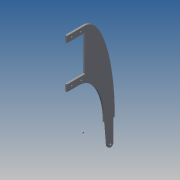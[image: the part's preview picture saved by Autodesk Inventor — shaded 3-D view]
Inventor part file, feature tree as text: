
AUTODESK INVENTOR PART (.ipt)
format: ipt  version: 2014 (Build 180170000, 170)  size: 110,592 bytes
history: native  units: mm
features: sketch x2, extrude x1
ambient origin geometry x8: Origin, YZ Plane, XZ Plane, XY Plane, X Axis, Y Axis, Z Axis, Center Point
bodies: Solid1 (feature_tree)
feature tree (3):
  sketch  "Sketch1"  dims[d0=106.0mm d5=33.5mm]
  sketch  "Sketch2"  dims[d6=106.0mm d10=20.5mm d12=28.5mm d14=6.5mm d15=7.0mm d16=40.5mm d17=1.5mm d18=1.5mm d22=3.5mm d23=5.0mm d24=1.5mm d25=1.5mm d26=5.5mm d27=1.5mm d28=5.5mm d29=1.5mm d32=25.0mm d34=24.5mm d35=6.5mm d36=2.0mm d37=2.0mm d38=0.0mm]
  extrude  "Extrusion1"  Depth=106.0mm
